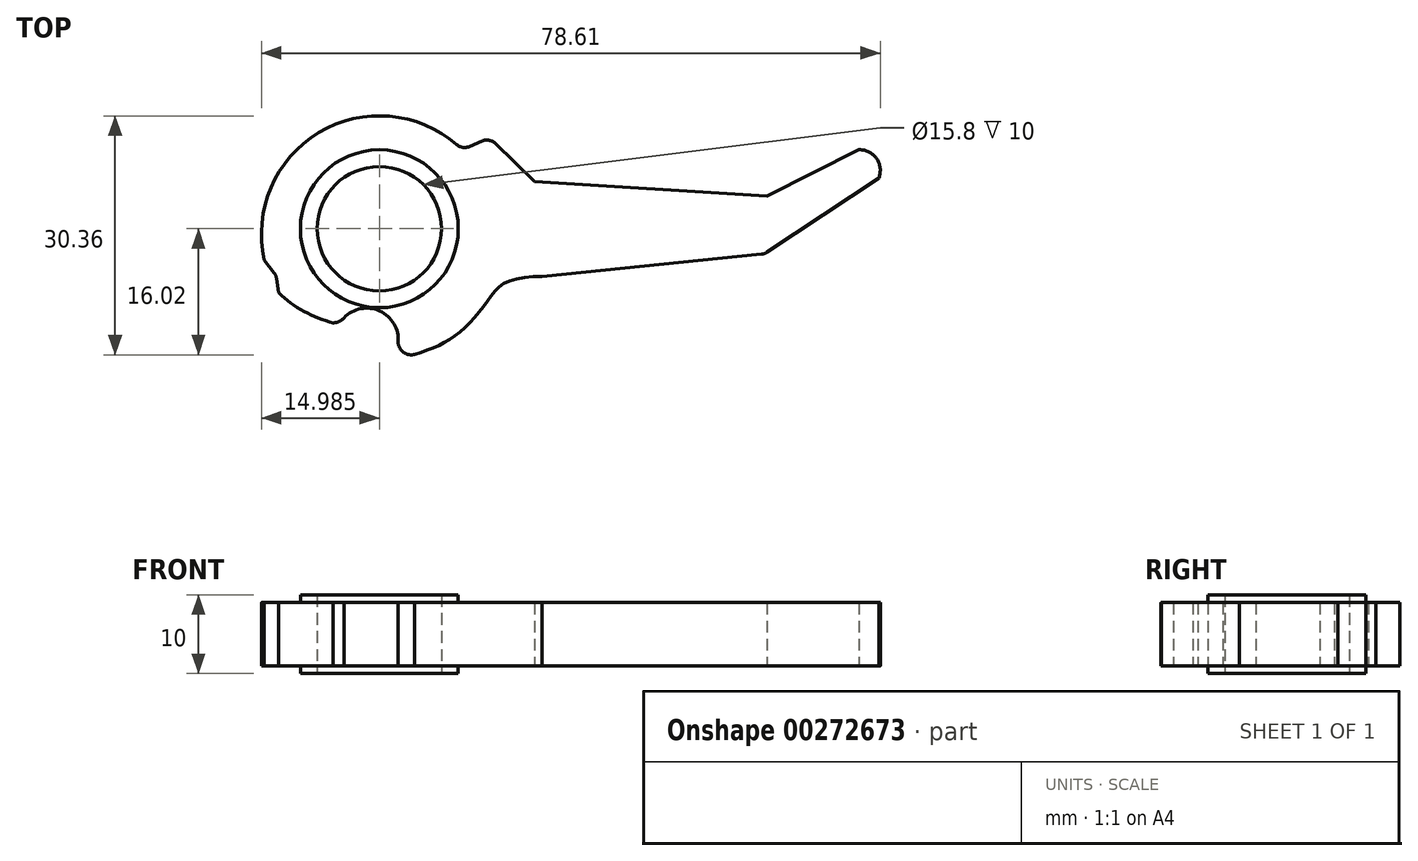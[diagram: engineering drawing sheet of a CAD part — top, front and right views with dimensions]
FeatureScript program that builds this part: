
annotation { "Feature Type Name" : "Feature", "Feature Type Description" : "" }
export const myFeature = defineFeature(function(context is Context, id is Id, definition is map)
    precondition{}
    {
        {
            var Q0;
            Q0=qCreatedBy(makeId("Top.planeOp"),FACE);
            var sketch = newSketch(context, id + "F0", { "sketchPlane" : qUnion([Q0])});
            skCircle(sketch, "E0", {"center": v(-3.07, 0.77) * mm, "radius": 7.9 * mm});
            skPoint(sketch, "E0.first.point", {"position": v(-0.32, -6.63) * mm});
            skPoint(sketch, "E0.second.point", {"position": v(-4.58, 8.52) * mm});
            skPoint(sketch, "E0.third.point", {"position": v(-10.45, -2.06) * mm});
            skLineSegment(sketch, "E1", {"start": v(16.67, 6.77) * mm, "end": v(46.15, 4.94) * mm});
            skLineSegment(sketch, "E2", {"start": v(46.15, 4.94) * mm, "end": v(57.88, 10.8) * mm});
            skLineSegment(sketch, "E3", {"start": v(16.67, 6.77) * mm, "end": v(10.88, 12.33) * mm});
            skLineSegment(sketch, "E4", {"start": v(10.88, 12.33) * mm, "end": v(7.45, 10.8) * mm});
            skArc(sketch, "E5", {"start": v(7.45, 10.8) * mm, "mid": v(-10.36, 13.21) * mm, "end": v(-17.69, -3.2) * mm});
            skLineSegment(sketch, "E6", {"start": v(-17.69, -3.2) * mm, "end": v(-16.19, -5.18) * mm});
            skLineSegment(sketch, "E7", {"start": v(-16.19, -5.18) * mm, "end": v(-15.88, -7.35) * mm});
            skArc(sketch, "E8", {"start": v(-15.88, -7.35) * mm, "mid": v(-12.66, -9.73) * mm, "end": v(-8.93, -11.19) * mm});
            skArc(sketch, "E9", {"start": v(-8.93, -11.19) * mm, "mid": v(-8.18, -11.02) * mm, "end": v(-7.57, -10.54) * mm});
            skArc(sketch, "E10", {"start": v(-0.69, -13.68) * mm, "mid": v(-3.02, -9.68) * mm, "end": v(-7.57, -10.54) * mm});
            skArc(sketch, "E11", {"start": v(-0.69, -13.68) * mm, "mid": v(0, -14.94) * mm, "end": v(1.4, -15.2) * mm});
            skFitSpline(sketch, "E12", {"points": [v(1.4, -15.2) * mm, v(3.94, -14.3) * mm, v(5.99, -13.2) * mm, v(8.16, -11.45) * mm, v(10.09, -9.2) * mm, v(11.69, -7.1) * mm, v(13.41, -5.88) * mm, v(17.58, -5.27) * mm], "startDerivative": vector(18.6, 6.02) * mm, "endDerivative": vector(25.16, 0.78) * mm});
            skLineSegment(sketch, "E13", {"start": v(17.58, -5.27) * mm, "end": v(45.84, -2.43) * mm});
            skLineSegment(sketch, "E14", {"start": v(45.84, -2.43) * mm, "end": v(60.38, 7.22) * mm});
            skArc(sketch, "E15", {"start": v(60.38, 7.22) * mm, "mid": v(60.08, 9.68) * mm, "end": v(57.88, 10.8) * mm});
            skSolve(sketch);
        }
        {
            var Q0;
            Q0 = qSketchRegion(id + "F0", true);
            extrude(context, id + "F1", {"entities" : qUnion([Q0]), "endBound" : BoundingType.SYMMETRIC, "depth" : 8.04 * mm});
        }
        {
            var Q0;
            Q0=qCreatedBy(makeId("Top.planeOp"),FACE);
            var sketch = newSketch(context, id + "F2", { "sketchPlane" : qUnion([Q0])});
            skCircle(sketch, "E16.0", {"center": v(-3.07, 0.77) * mm, "radius": 7.9 * mm});
            skCircle(sketch, "E17.0", {"center": v(-3.07, 0.77) * mm, "radius": 10.03 * mm});
            skSolve(sketch);
        }
        {
            var Q0;
            Q0=makeQuery(id+"F2.imprint","IMPRINT",FACE,{"disambiguationData":[TD([[makeQuery(id+"F2.imprint","IMPRINT",EDGE,{"derivedFrom":sQuery(id+"F2.wireOp",EDGE,"E16.0")}),-1.0]])]});
            extrude(context, id + "F3", {"entities" : qUnion([Q0]), "operationType" : NewBodyOperationType.ADD, "endBound" : BoundingType.SYMMETRIC, "depth" : 10 * mm});
        }
        {
            var Q0;
            Q0=makeQuery(id+"F1.opExtrude","SWEPT_EDGE",EDGE,{"disambiguationData":[OSD([sQuery(id+"F0.wireOp",EDGE,"E6"),sQuery(id+"F0.wireOp",EDGE,"E7")])]});
            var Q1;
            Q1=makeQuery(id+"F1.opExtrude","SWEPT_EDGE",EDGE,{"disambiguationData":[OSD([sQuery(id+"F0.wireOp",EDGE,"E4"),sQuery(id+"F0.wireOp",EDGE,"E5")])]});
            var Q2;
            Q2=makeQuery(id+"F1.opExtrude","SWEPT_EDGE",EDGE,{"disambiguationData":[OSD([sQuery(id+"F0.wireOp",EDGE,"E3"),sQuery(id+"F0.wireOp",EDGE,"E4")])]});
            var Q3;
            Q3=makeQuery(id+"F1.opExtrude","SWEPT_EDGE",EDGE,{"disambiguationData":[OSD([sQuery(id+"F0.wireOp",EDGE,"E13"),sQuery(id+"F0.wireOp",EDGE,"E14")])]});
            fillet(context, id + "F4", {"entities" : qUnion([Q0, Q1, Q2, Q3]), "radius" : 1.52 * mm, "tangentPropagation" : true, "allowEdgeOverflow" : false});
        }
    });
